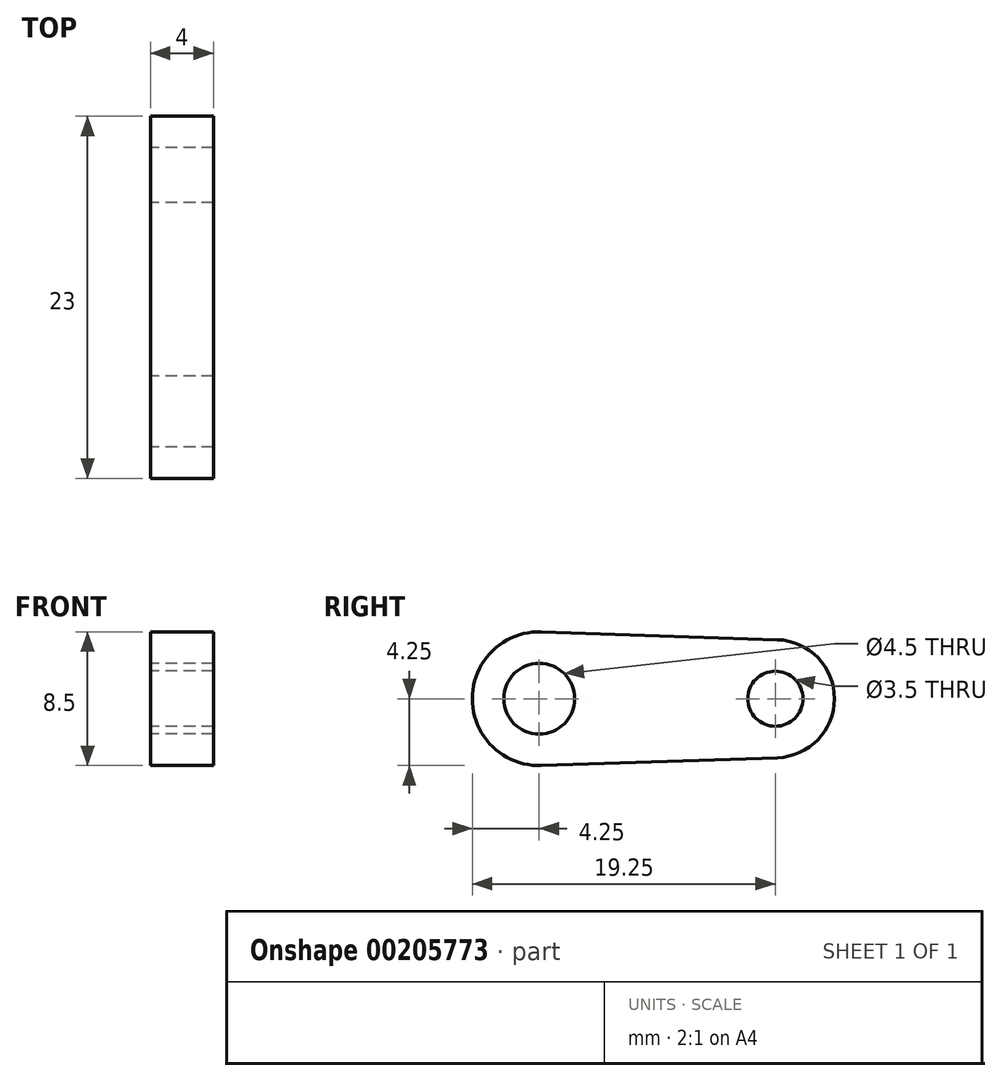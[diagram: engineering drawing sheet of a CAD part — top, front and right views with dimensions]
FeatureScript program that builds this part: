
annotation { "Feature Type Name" : "Feature", "Feature Type Description" : "" }
export const myFeature = defineFeature(function(context is Context, id is Id, definition is map)
    precondition{}
    {
        {
            var Q0;
            Q0=qCreatedBy(makeId("Right.planeOp"),FACE);
            var sketch = newSketch(context, id + "F0", { "sketchPlane" : qUnion([Q0])});
            skLineSegment(sketch, "E0", {"start": v(0, 0) * mm, "end": v(15, 0) * mm, "construction": true});
            skSolve(sketch);
        }
        {
            var Q0;
            Q0=qCreatedBy(makeId("Right.planeOp"),FACE);
            var sketch = newSketch(context, id + "F1", { "sketchPlane" : qUnion([Q0])});
            skCircle(sketch, "E1", {"center": v(0, 0) * mm, "radius": 2.25 * mm});
            skCircle(sketch, "E2", {"center": v(15, 0) * mm, "radius": 1.75 * mm});
            skArc(sketch, "E3", {"start": v(0.14, 4.25) * mm, "mid": v(-4.25, 0) * mm, "end": v(0.14, -4.25) * mm});
            skArc(sketch, "E4", {"start": v(15.13, -3.75) * mm, "mid": v(18.75, 0) * mm, "end": v(15.12, 3.75) * mm});
            skLineSegment(sketch, "E5", {"start": v(0.14, 4.25) * mm, "end": v(15.12, 3.75) * mm});
            skLineSegment(sketch, "E6.MirrorCS", {"start": v(0.14, -4.25) * mm, "end": v(15.12, -3.75) * mm});
            skSolve(sketch);
        }
        {
            var Q0;
            Q0 = qSketchRegion(id + "F1", true);
            extrude(context, id + "F2", {"entities" : qUnion([Q0]), "depth" : 4 * mm});
        }
    });
